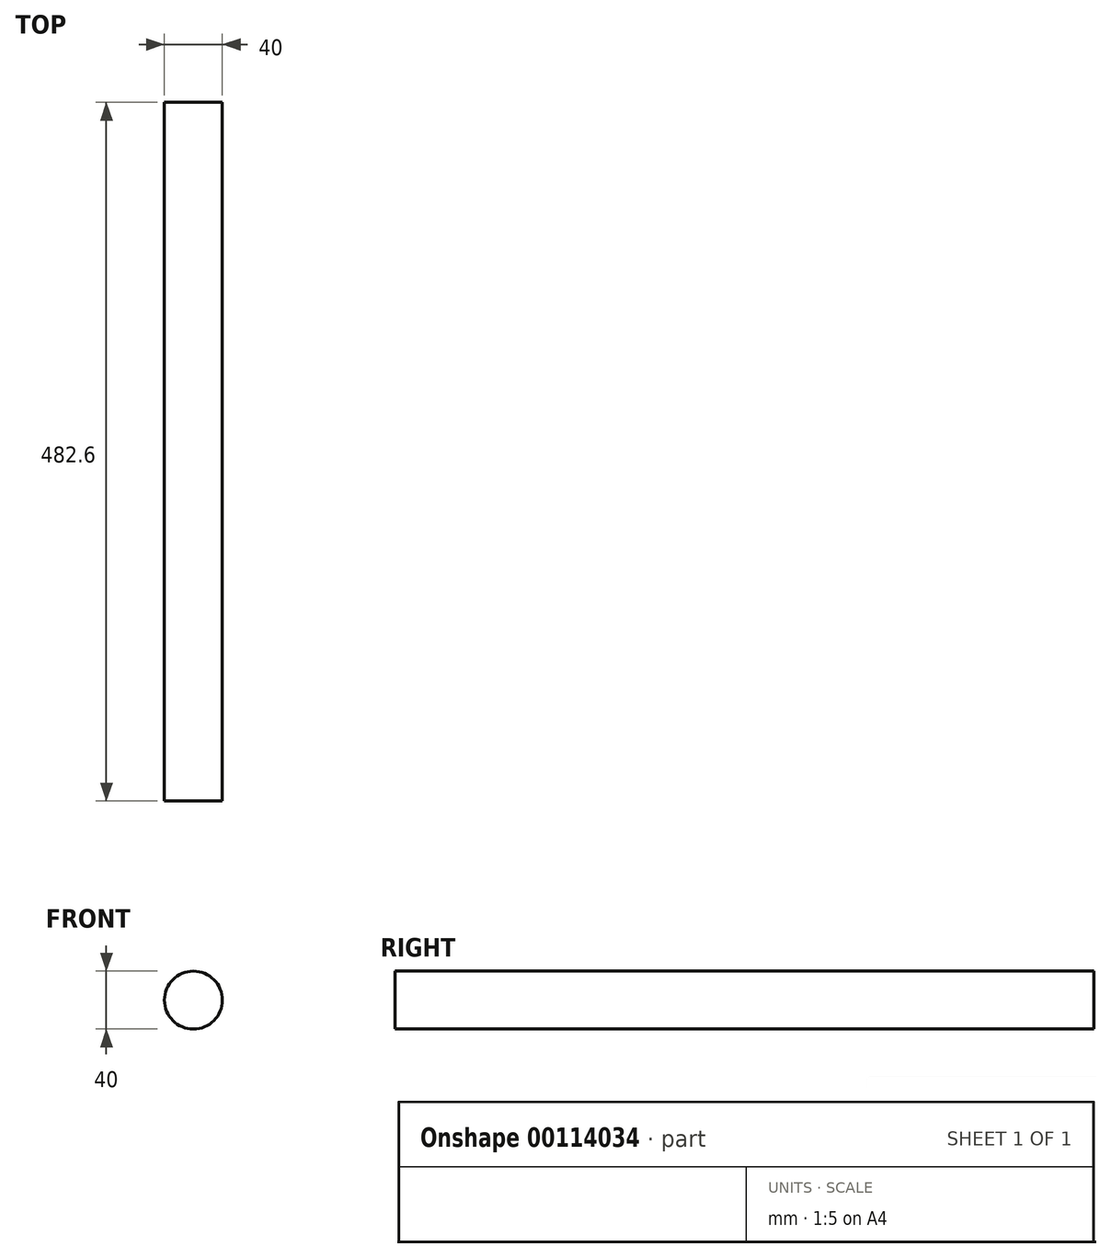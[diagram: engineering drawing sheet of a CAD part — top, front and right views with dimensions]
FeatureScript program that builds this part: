
annotation { "Feature Type Name" : "Feature", "Feature Type Description" : "" }
export const myFeature = defineFeature(function(context is Context, id is Id, definition is map)
    precondition{}
    {
        {
            var Q0;
            Q0=qCreatedBy(makeId("Front.planeOp"),FACE);
            var sketch = newSketch(context, id + "F0", { "sketchPlane" : qUnion([Q0])});
            skCircle(sketch, "E0", {"center": v(0, 0) * mm, "radius": 20 * mm});
            skSolve(sketch);
        }
        {
            var Q0;
            Q0 = qSketchRegion(id + "F0", true);
            extrude(context, id + "F1", {"entities" : qUnion([Q0]), "endBound" : BoundingType.SYMMETRIC, "depth" : 482.6 * mm});
        }
    });
